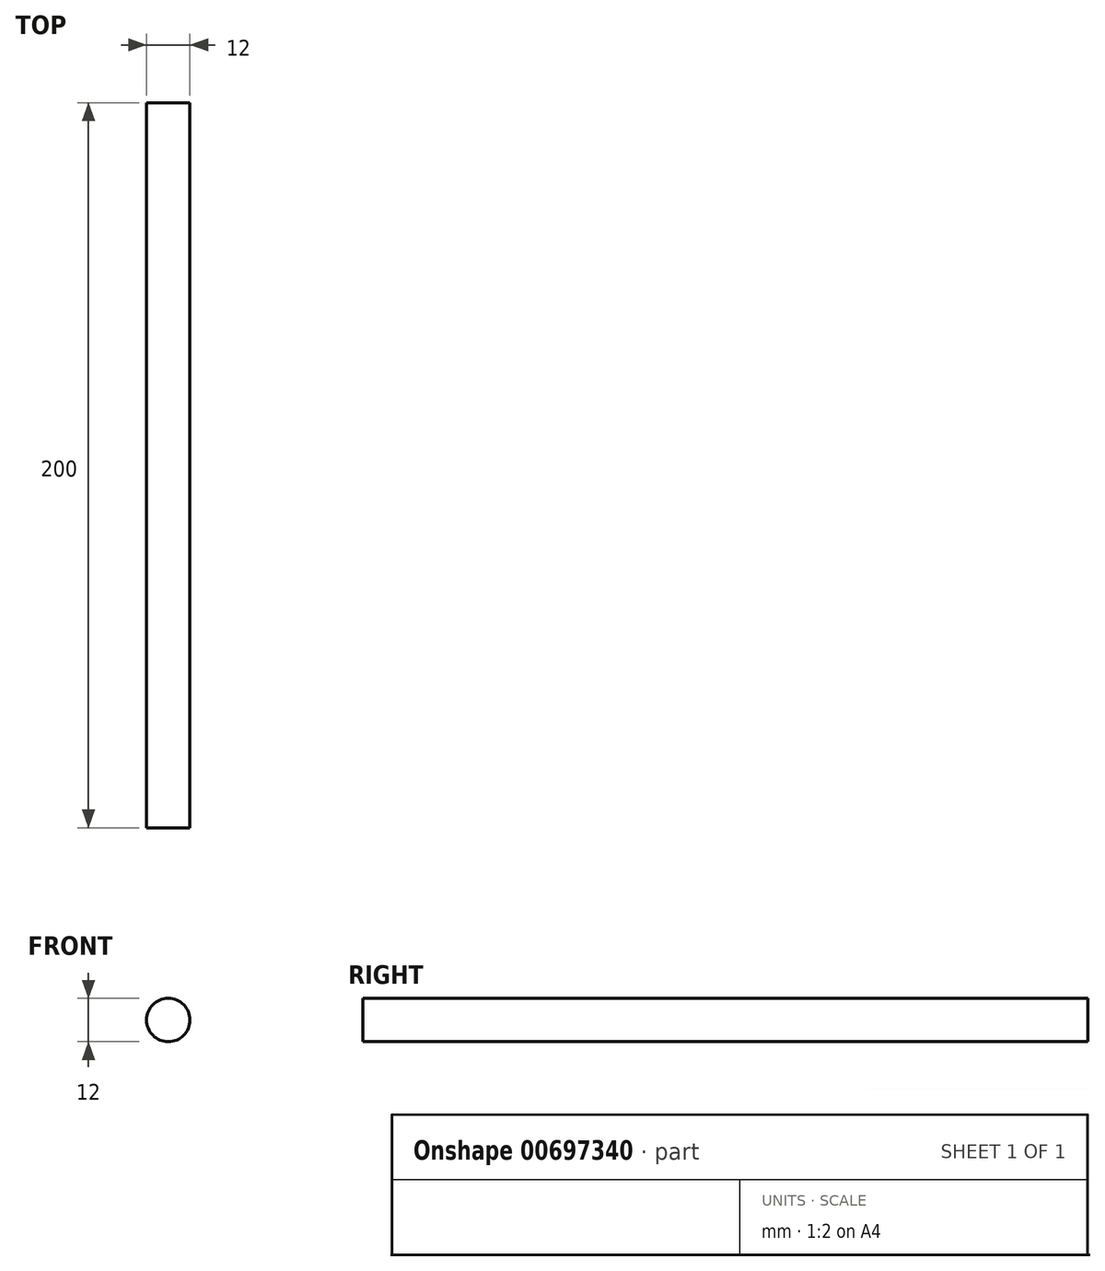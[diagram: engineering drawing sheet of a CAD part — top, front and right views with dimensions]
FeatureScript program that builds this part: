
annotation { "Feature Type Name" : "Feature", "Feature Type Description" : "" }
export const myFeature = defineFeature(function(context is Context, id is Id, definition is map)
    precondition{}
    {
        {
            var Q0;
            Q0=qCreatedBy(makeId("Front.planeOp"),FACE);
            var sketch = newSketch(context, id + "F0", { "sketchPlane" : qUnion([Q0])});
            skCircle(sketch, "E0", {"center": v(0, 0) * mm, "radius": 6 * mm});
            skSolve(sketch);
        }
        {
            var Q0;
            Q0 = qSketchRegion(id + "F0", true);
            extrude(context, id + "F1", {"entities" : qUnion([Q0]), "depth" : 200 * mm, "offsetDistance" : 25 * mm});
        }
    });
